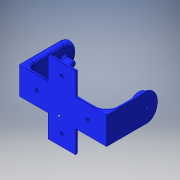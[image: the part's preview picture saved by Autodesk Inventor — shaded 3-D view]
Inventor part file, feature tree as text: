
AUTODESK INVENTOR PART (.ipt)
format: ipt  version: 2016 (Build 200138000, 138)  size: 381,440 bytes
history: native  units: in
note: dims shown in document units (in); Inventor stores cm internally (conversion verified against a paired STEP export)
features: sketch x11, other x3
ambient origin geometry x8: Origin, YZ Plane, XZ Plane, XY Plane, X Axis, Y Axis, Z Axis, Center Point
bodies: Solid1 (feature_tree)
feature tree (14):
  other  "Hip_side.ipt"
  other  "Solid1::Hip_side.ipt"
  other  "TaggingFeature1"
  sketch  "Sketch1"  dims[d0=0.3937in]
  sketch  "Sketch4"
  sketch  "Sketch5"
  sketch  "Sketch7"
  sketch  "Sketch9"
  sketch  "Sketch10"
  sketch  "Sketch15"
  sketch  "Sketch16"
  sketch  "Sketch17"
  sketch  "Sketch18"
  sketch  "Sketch19"
